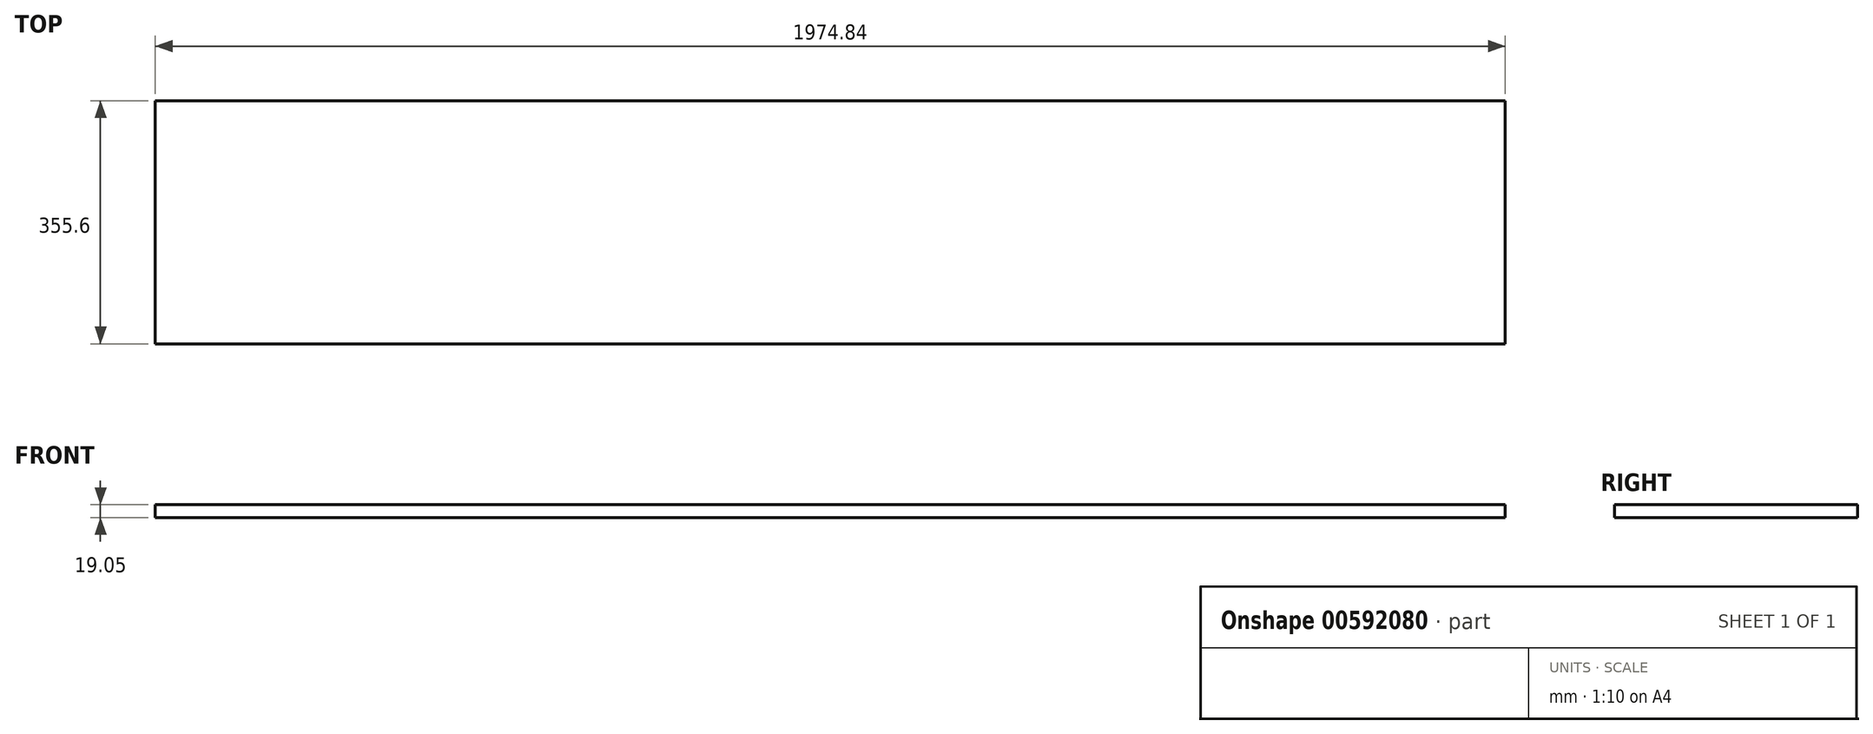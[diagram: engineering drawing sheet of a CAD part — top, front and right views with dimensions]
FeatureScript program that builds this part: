
annotation { "Feature Type Name" : "Feature", "Feature Type Description" : "" }
export const myFeature = defineFeature(function(context is Context, id is Id, definition is map)
    precondition{}
    {
        {
            var Q0;
            Q0=qCreatedBy(makeId("Top.planeOp"),FACE);
            var sketch = newSketch(context, id + "F0", { "sketchPlane" : qUnion([Q0])});
            skLineSegment(sketch, "E0.bottom", {"start": v(987.43, 177.8) * mm, "end": v(-987.43, 177.8) * mm});
            skLineSegment(sketch, "E0.top", {"start": v(987.43, -177.8) * mm, "end": v(-987.43, -177.8) * mm});
            skLineSegment(sketch, "E0.left", {"start": v(987.43, 177.8) * mm, "end": v(987.43, -177.8) * mm});
            skLineSegment(sketch, "E0.right", {"start": v(-987.43, 177.8) * mm, "end": v(-987.43, -177.8) * mm});
            skPoint(sketch, "E0.middle", {"position": v(0, 0) * mm});
            skSolve(sketch);
        }
        {
            var Q0;
            Q0=makeQuery(id+"F0.imprint","IMPRINT",FACE,{"disambiguationData":[TD([[makeQuery(id+"F0.imprint","IMPRINT",EDGE,{"derivedFrom":sQuery(id+"F0.wireOp",EDGE,"E0.bottom")}),1.0]])]});
            extrude(context, id + "F1", {"entities" : qUnion([Q0]), "depth" : 19.05 * mm, "offsetDistance" : 25.4 * mm});
        }
    });
